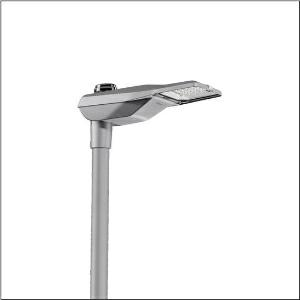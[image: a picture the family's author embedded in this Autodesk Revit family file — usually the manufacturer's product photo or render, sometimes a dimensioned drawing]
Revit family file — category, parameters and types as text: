
# Revit family: streetlight_sl_21_micro___st1_5a_5xe5p47n08cb_4c70
name_source: partatom
category: Lighting Fixtures
units: mm (PartAtom-declared; Revit-internal decimal feet)

## family parameters
Cut with Voids When Loaded = No
Host = Face
Light Source = No
Part Type = Normal
Room Calculation Point = No
Round Connector Dimension = Use Diameter
Shared = No

## types (1)
- --- (1 x LED, 2340 lm, 15.8 W, 4000K)
    Apparent Load = 16 VA
    CIE Flux Codes = 22 53 95 100 100
    Color Rendering = 70
    Color Temperature = 4000K
    Default Elevation = 1800 mm
    Description = Streetlight SL 21 micro, mast luminaire, primary light control with lens, of PMMA, primary optical cover: cover, of toughened safety glass, transparent, light distribution: ST1.5a, light emission: direct distribution, primary light characteristic: asymmetric, installation type: post-top, LED, 3G 1.5mm², High Power LED, rated luminous flux: 2.340lm, luminous efficacy: 148lm/W, light colour: 740, colour temperature: 4000K, control gear: NEMA (7pin), control: overheat protection, pre-setting: linear dimming characteristic, constant luminous flux control, time-dependent luminous flux control, flexible luminous flux parameterisation, mains connection: 230..240V, AC, 50/60Hz, connection cable pre-assembled, cable length: 6,5m, wiring characteristics: H07RN-F, start of lifetime: 16W, end of service life: 16W, reduction: 8W, luminaire housing, of diecast aluminium (EN AC-44300), powder-coated, Siteco® metallic grey (DB 702S), corrosivity category C5 mid according to DIN EN ISO 12944, multi-level sealing system, sealing non-destructively replaceable, inclination adjustable: 0°, 5°, 10°, 15°, length: 528mm, width: 235mm, height: 110mm, spigot size: 76/60mm (post-top), mounting height: 4..8m, protection rating (complete): IP66, insulation class (complete): insulation class I (protective earthing), certification: CE, ENEC, ENEC+, VDE, impact resistance: IK09, permissible operating ambient temperature for outdoor applications: -40..+50°C, standard-compliant lighting for roads and squares, packaging unit: 1 piece

Light Distribution: ST1.5a
    Height = 110 mm
    Lamp = 1 x LED
    Lamp Light Flux = 2340 lm
    Lamp Power = 15.8 W
    Lamp count = 1
    Length = 528 mm
    Luminous efficacy = 148 lm/W
    Manufacturer = Siteco
    ModVariant = No
    Model = 5XE5P47N08CB
    Number of Poles = 1
    OnlyDefault = Yes
    Power Factor = 1
    Product Name = Streetlight SL 21 micro | ST1.5a
    Product group = mast luminaire | pylon top
    ProductGroupID = 6100
    Protection Class = Protection class I
    Protection Degree = IP 66
    RLX_Detail_Level = 1
    RLX_Emergency_Light_Flux = 0 lm
    RLX_Emergency_Type = 0
    RLX_Emergency_Type_DB = No
    RlxData = <blob elided: 102477 chars, md5=7e14a8ef>
    Socket = socket
    Standby Power = 0 W
    System Light Flux = 2340 lm
    System Power = 16 W
    Type Comments = factory setting: luminous flux: 100 % | dim-lin: 254 | 300 mA
    Type Image = l_1294375.jpg
    URL = http://relux.com
    VarID = @adj_129040
    Voltage = 0 V
    Weight = 0.00 kg
    Width = 235 mm

## geometry (parser evidence)
native form markers: Blend x4, Sweep x11
no freeform markers — native parametric forms only
